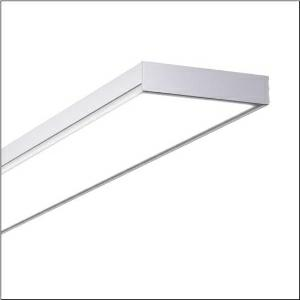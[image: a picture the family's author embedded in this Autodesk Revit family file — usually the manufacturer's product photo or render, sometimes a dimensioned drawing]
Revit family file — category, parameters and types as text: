
# Revit family: apollon_31_surface_51mp25wd2441ea
name_source: partatom
category: Lighting Fixtures
units: mm (PartAtom-declared; Revit-internal decimal feet)

## family parameters
Cut with Voids When Loaded = No
Host = Face
Light Source = No
Part Type = Normal
Room Calculation Point = No
Round Connector Dimension = Use Diameter
Shared = No

## types (1)
- Apollon 31 Surface (1 x LED, 3800 lm, 28 W, 4000K)
    Apparent Load = 28 VA
    CIE Flux Codes = 61 87 97 97 100
    Color Rendering = 80
    Color Temperature = 4000K
    Default Elevation = 1800 mm
    Description = Apollon 31 Surface, office luminaire, primary optical cover: micro prismatic cover, of PMMA, light emission: direct distribution, primary light characteristic: symmetric, installation type: surface-mounted, LED, rated luminous flux: 3.800lm, luminous efficacy: 134lm/W, light colour: 840, colour temperature: 4000K, control gear: DALI 2, with terminal, 5-pole, mains connection: 220..240V, AC, 50/60Hz, rated input power: 28W, housing, of sheet steel, coated, metallic grey (RAL 9006), length: 1.245mm, width: 200mm, height: 44mm, protection rating (complete): IP20, protection rating (on room side): IP40, protection rating (lamp compartment, on room side): IP40, insulation class (complete): insulation class I (protective earthing), certification: CE, ENEC, UKCA, impact resistance: IK02, permissible operating ambient temperature: -20..+40°C, standard: EN 60598-2-22, packaging unit: 1 piece
    Height = 44 mm
    Lamp = 1 x LED
    Lamp Light Flux = 3800 lm
    Lamp Power = 28 W
    Lamp count = 1
    Length = 1245 mm
    Luminous efficacy = 136 lm/W
    Manufacturer = Siteco
    ModVariant = No
    Model = 51MP25WD2441EA
    Mounting Place = Ceiling
    Mounting Type = Surface mounted
    Number of Poles = 1
    OnlyDefault = Yes
    Power Factor = 1
    Product Name = Apollon 31 Surface
    Product group = office luminaire | ceiling mounted
    ProductGroupID = 301
    Protection Class = Protection class I
    Protection Degree = IP 20
    RLX_Detail_Level = 1
    RLX_Emergency_Light_Flux = 0 lm
    RLX_Emergency_Type = 0
    RLX_Emergency_Type_DB = No
    RlxData = <blob elided: 24129 chars, md5=b7a63f41>
    Socket = socket
    Standby Power = 0 W
    System Light Flux = 3800 lm
    System Power = 28 W
    Type Comments = Product without accessories
    Type Image = l_1313654.jpg
    URL = http://relux.com
    VarID = ---
    Voltage = 0 V
    Weight = 0.00 kg
    Width = 200 mm  [stored 0.656168 ft]

note: [stored X ft] marks values corroborated as IEEE doubles in the binary element streams (Revit-internal decimal feet)

## geometry (parser evidence)
native form markers: Blend x4, Sweep x9
no freeform markers — native parametric forms only
